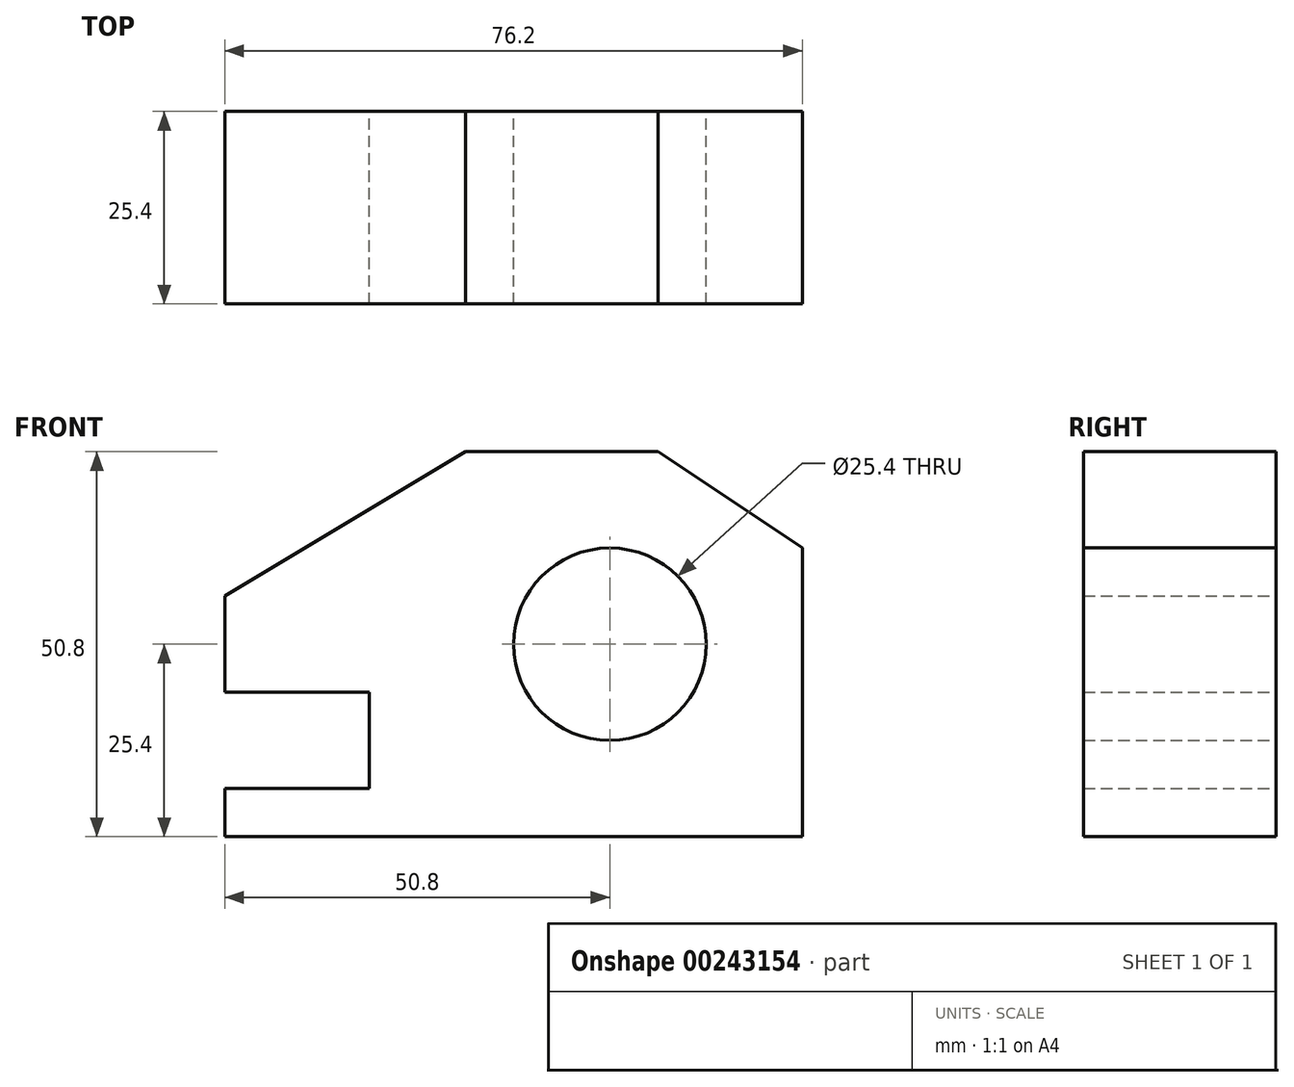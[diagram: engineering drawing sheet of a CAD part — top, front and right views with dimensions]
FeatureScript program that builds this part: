
annotation { "Feature Type Name" : "Feature", "Feature Type Description" : "" }
export const myFeature = defineFeature(function(context is Context, id is Id, definition is map)
    precondition{}
    {
        {
            var Q0;
            Q0=qCreatedBy(makeId("Front.planeOp"),FACE);
            var sketch = newSketch(context, id + "F0", { "sketchPlane" : qUnion([Q0])});
            skLineSegment(sketch, "E0", {"start": v(-19.05, 25.4) * mm, "end": v(6.35, 25.4) * mm});
            skLineSegment(sketch, "E1", {"start": v(6.35, 25.4) * mm, "end": v(25.4, 12.7) * mm});
            skLineSegment(sketch, "E2", {"start": v(25.4, 12.7) * mm, "end": v(25.4, -25.4) * mm});
            skLineSegment(sketch, "E3", {"start": v(25.4, -25.4) * mm, "end": v(-50.8, -25.4) * mm});
            skLineSegment(sketch, "E4", {"start": v(-50.8, -25.4) * mm, "end": v(-50.8, -19.05) * mm});
            skLineSegment(sketch, "E5", {"start": v(-50.8, -19.05) * mm, "end": v(-31.75, -19.05) * mm});
            skLineSegment(sketch, "E6", {"start": v(-31.75, -19.05) * mm, "end": v(-31.75, -6.35) * mm});
            skLineSegment(sketch, "E7", {"start": v(-31.75, -6.35) * mm, "end": v(-50.8, -6.35) * mm});
            skLineSegment(sketch, "E8", {"start": v(-50.8, -6.35) * mm, "end": v(-50.8, 6.35) * mm});
            skLineSegment(sketch, "E9", {"start": v(-50.8, 6.35) * mm, "end": v(-19.05, 25.4) * mm});
            skCircle(sketch, "E10", {"center": v(0, 0) * mm, "radius": 12.7 * mm});
            skSolve(sketch);
        }
        {
            var Q0;
            Q0 = qSketchRegion(id + "F0", true);
            extrude(context, id + "F1", {"entities" : qUnion([Q0]), "depth" : 25.4 * mm});
        }
    });
